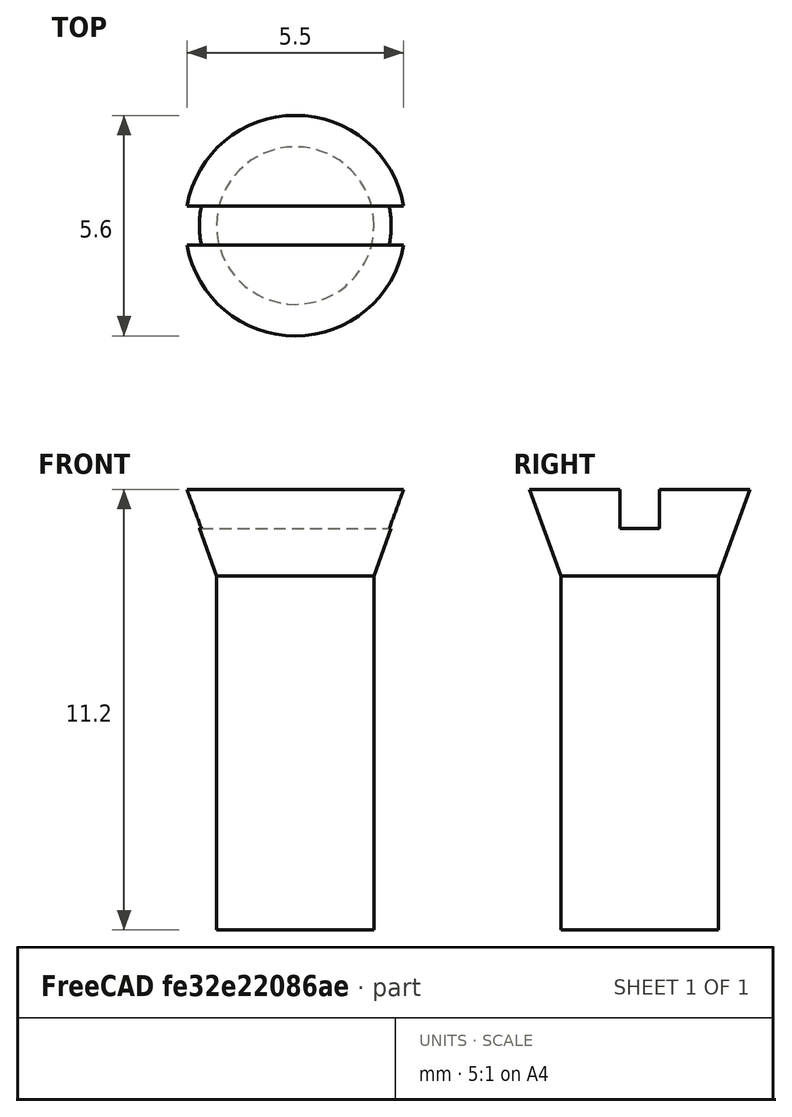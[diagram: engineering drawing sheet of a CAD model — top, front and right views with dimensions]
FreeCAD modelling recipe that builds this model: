
FCSTD DOCUMENT  (FreeCAD 1.0R39319 (Git))
Label: ojt1_t14r01_screw
License: All rights reserved
LicenseURL: https://en.wikipedia.org/wiki/All_rights_reserved
objects: Part::Cylinder×1, Part::Cone×1, Part::Box×1, Part::Cut×1, Part::MultiFuse×1
note: 5 computed .brp shape members not serialized (recipe doc carries the construction recipe); baked Part::Feature solids carry a one-line shape summary decoded from their .brp

FEATURE [Part::Cylinder] Cylinder  label="Cilindre"
  Angle = 360
  AttacherType = Attacher::AttachEngine3D
  FirstAngle = 0
  Height = 10
  Radius = 2
  SecondAngle = 0
FEATURE [Part::Cone] Cone  label="Con"
  Angle = 360
  AttacherType = Attacher::AttachEngine3D
  Height = 2.2
  Placement = pos=(0,0,9) rot=(0,0,1;0rad)
  Radius1 = 2
  Radius2 = 2.8
FEATURE [Part::Box] Box  label="Cub"
  AttacherType = Attacher::AttachEngine3D
  Height = 1
  Length = 10
  Placement = pos=(-4,-0.5,10.2) rot=(0,0,1;0rad)
  Width = 1
FEATURE [Part::Cut] Cut
  Base = -> Cone
  Tool = -> Box
FEATURE [Part::MultiFuse] Fusion  label="clau"
  Shapes = -> [Cylinder,Cut]
